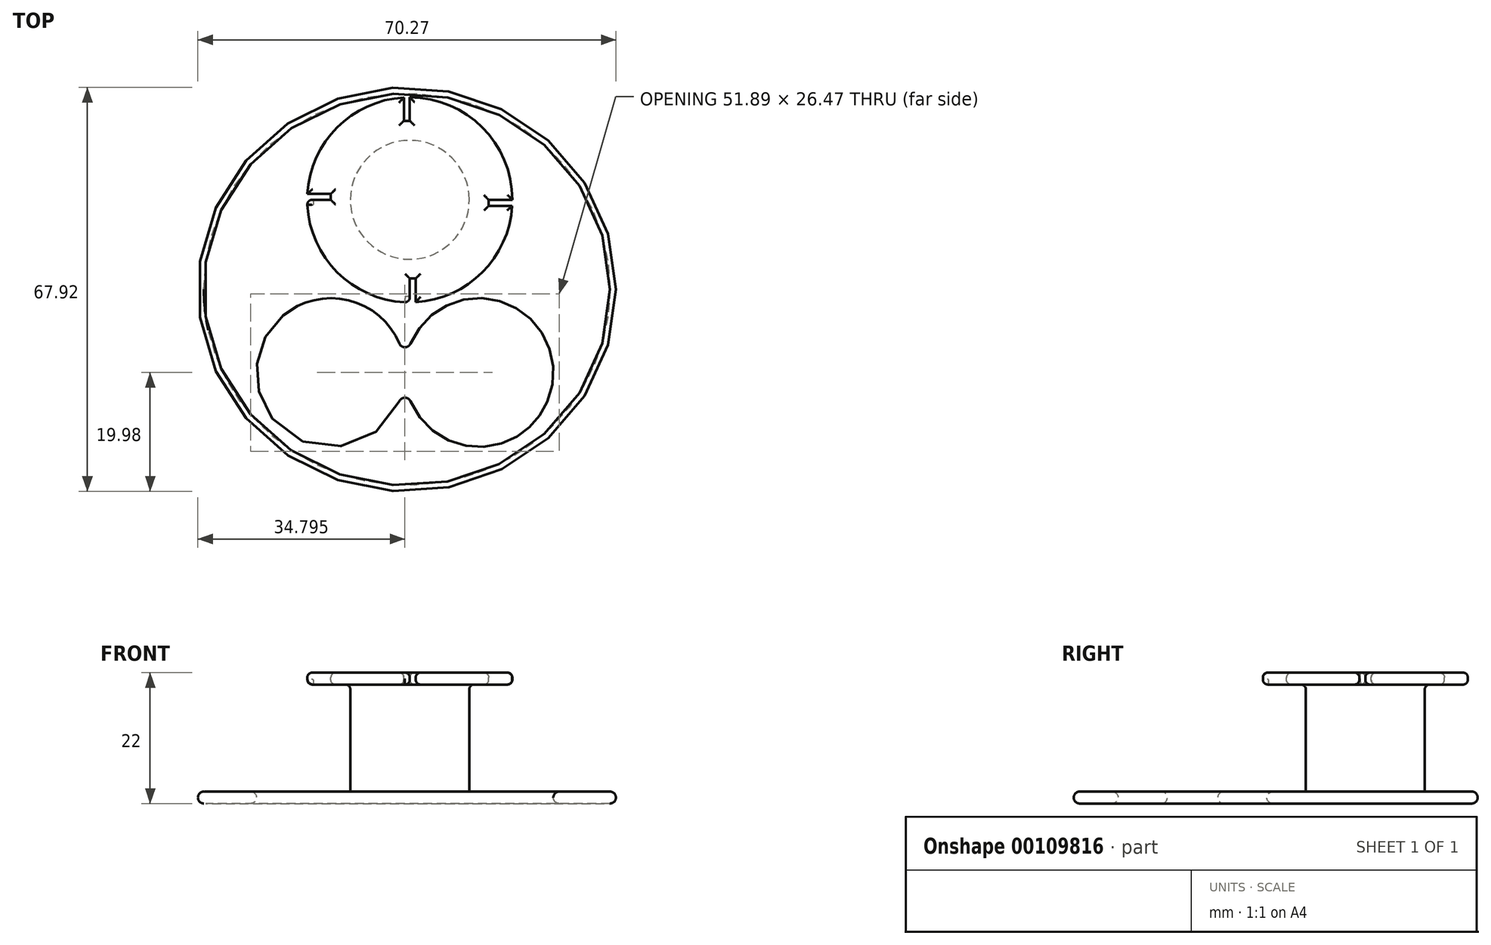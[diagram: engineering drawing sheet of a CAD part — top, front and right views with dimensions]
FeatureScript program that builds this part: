
annotation { "Feature Type Name" : "Feature", "Feature Type Description" : "" }
export const myFeature = defineFeature(function(context is Context, id is Id, definition is map)
    precondition{}
    {
        {
            var Q0;
            Q0=qCreatedBy(makeId("Top.planeOp"),FACE);
            var sketch = newSketch(context, id + "F0", { "sketchPlane" : qUnion([Q0])});
            skCircle(sketch, "E0", {"center": v(0, 0) * mm, "radius": 12.5 * mm});
            skCircle(sketch, "E1", {"center": v(24.89, 0) * mm, "radius": 12.5 * mm});
            skPoint(sketch, "E2.center.orphan", {"position": v(48.98, 0) * mm});
            skEllipse(sketch, "E3", {"center": v(12.79, 13.98) * mm, "majorRadius": 35.13 * mm, "minorRadius": 33.96 * mm, "majorAxis": v(1, 0)});
            skSolve(sketch);
        }
        {
            var Q0;
            Q0 = qSketchRegion(id + "F0", true);
            extrude(context, id + "F1", {"entities" : qUnion([Q0]), "depth" : 2 * mm});
        }
        {
            var Q0;
            Q0=makeQuery(id+"F1.opExtrude","CAP_FACE",FACE,{"disambiguationData":[OSD([sQuery(id+"F0.wireOp",EDGE,"E0"),sQuery(id+"F0.wireOp",EDGE,"E1"),sQuery(id+"F0.wireOp",EDGE,"E3")])],"isStart":false});
            var sketch = newSketch(context, id + "F2", { "sketchPlane" : qUnion([Q0])});
            skCircle(sketch, "E4", {"center": v(13.26, 29.04) * mm, "radius": 10 * mm});
            skSolve(sketch);
        }
        {
            var Q0;
            Q0 = qSketchRegion(id + "F2", true);
            extrude(context, id + "F3", {"entities" : qUnion([Q0]), "operationType" : NewBodyOperationType.ADD, "depth" : 20 * mm});
        }
        {
            var Q0;
            Q0=makeQuery(id+"F3.opExtrude","CAP_FACE",FACE,{"disambiguationData":[OSD([sQuery(id+"F2.wireOp",EDGE,"E4")])],"isStart":false});
            var sketch = newSketch(context, id + "F4", { "sketchPlane" : qUnion([Q0])});
            skArc(sketch, "E5", {"start": v(-3.97, 29.04) * mm, "mid": v(1.08, 16.85) * mm, "end": v(13.26, 11.8) * mm});
            skLineSegment(sketch, "E6.top", {"start": v(12.26, 42.33) * mm, "end": v(13.26, 42.33) * mm});
            skLineSegment(sketch, "E6.left", {"start": v(12.26, 46.25) * mm, "end": v(12.26, 42.33) * mm});
            skLineSegment(sketch, "E6.right", {"start": v(13.26, 46.16) * mm, "end": v(13.26, 42.28) * mm});
            skLineSegment(sketch, "E7.bottom", {"start": v(-3.94, 30.04) * mm, "end": v(0, 30.04) * mm});
            skLineSegment(sketch, "E7.top", {"start": v(-3.97, 29.04) * mm, "end": v(0, 29.04) * mm});
            skLineSegment(sketch, "E7.right", {"start": v(0, 30.04) * mm, "end": v(0, 29.04) * mm});
            skLineSegment(sketch, "E8.bottom", {"start": v(13.26, 15.8) * mm, "end": v(14.26, 15.8) * mm});
            skLineSegment(sketch, "E8.left", {"start": v(13.26, 15.8) * mm, "end": v(13.26, 11.8) * mm});
            skLineSegment(sketch, "E8.right", {"start": v(14.26, 15.8) * mm, "end": v(14.26, 11.83) * mm});
            skLineSegment(sketch, "E9.bottom", {"start": v(30.54, 29.04) * mm, "end": v(26.54, 29.04) * mm});
            skLineSegment(sketch, "E9.top", {"start": v(30.54, 28.04) * mm, "end": v(26.54, 28.04) * mm});
            skLineSegment(sketch, "E9.left", {"start": v(30.54, 29.04) * mm, "end": v(30.54, 28.04) * mm});
            skLineSegment(sketch, "E9.right", {"start": v(26.54, 29.04) * mm, "end": v(26.54, 28.04) * mm});
            skLineSegment(sketch, "E10", {"start": v(13.26, 29.04) * mm, "end": v(35.63, 29.04) * mm, "construction": true});
            skLineSegment(sketch, "E11", {"start": v(13.26, 29.04) * mm, "end": v(-2120.93, 29.04) * mm, "construction": true});
            skPoint(sketch, "E11.endSnap0", {"position": v(-4, 29.04) * mm});
            skLineSegment(sketch, "E12", {"start": v(13.26, 29.04) * mm, "end": v(13.26, 9.5) * mm, "construction": true});
            skLineSegment(sketch, "E13", {"start": v(13.26, 29.04) * mm, "end": v(13.26, 49.38) * mm, "construction": true});
            skLineSegment(sketch, "E14", {"start": v(13.26, 42.33) * mm, "end": v(13.26, 46.28) * mm});
            skLineSegment(sketch, "E15", {"start": v(12.16, 46.28) * mm, "end": v(12.26, 46.25) * mm});
            skLineSegment(sketch, "E16", {"start": v(-3.97, 29.04) * mm, "end": v(-3.97, 29.04) * mm});
            skArc(sketch, "E17.trimOffspring", {"start": v(30.5, 29.04) * mm, "mid": v(25.45, 41.23) * mm, "end": v(13.26, 46.28) * mm});
            skArc(sketch, "E18.trimOffspring", {"start": v(12.26, 46.25) * mm, "mid": v(1.08, 41.23) * mm, "end": v(-3.94, 30.04) * mm});
            skArc(sketch, "E19.trimOffspring", {"start": v(14.26, 11.83) * mm, "mid": v(25.45, 16.85) * mm, "end": v(30.47, 28.04) * mm});
            skSolve(sketch);
        }
        {
            var Q0;
            {var subQ6=sQuery(id+"F4.wireOp",EDGE,"E6.top");Q0=makeQuery(id+"F4.imprint","IMPRINT",FACE,{"disambiguationData":[TD([[makeQuery(id+"F4.imprint","IMPRINT",EDGE,{"derivedFrom":subQ6}),-1.0]])]});}
            extrude(context, id + "F5", {"entities" : qUnion([Q0]), "operationType" : NewBodyOperationType.ADD, "oppositeDirection" : true, "depth" : 2 * mm});
        }
        {
            var Q0;
            Q0=makeQuery(id+"F5.opExtrude","CAP_EDGE",EDGE,{"disambiguationData":[OSD([sQuery(id+"F2.wireOp",EDGE,"E4")])],"isStart":false});
            var Q1;
            {var subQ0=sQuery(id+"F4.wireOp",EDGE,"E5");Q1=makeQuery(id+"F5.opExtrude","CAP_EDGE",EDGE,{"disambiguationData":[OSD([subQ0]),TDD([makeQuery(id+"F4.imprint","IMPRINT",EDGE,{"disambiguationData":[TD([[makeQuery(id+"F4.imprint","INTERSECT",VERTEX,{"derivedFrom":[subQ0,sQuery(id+"F4.wireOp",EDGE,"E6.left"),sQuery(id+"F4.wireOp",EDGE,"E15")]}),-1.0]])],"derivedFrom":subQ0})])],"isStart":false});}
            var Q2;
            {var subQ0=sQuery(id+"F0.wireOp",EDGE,"E1");var subQ1=sQuery(id+"F0.wireOp",EDGE,"E0");Q2=makeQuery(id+"F1.opExtrude","SWEPT_EDGE",EDGE,{"disambiguationData":[OSD([subQ1,subQ0]),TDD([makeQuery(id+"F0.imprint","INTERSECT",VERTEX,{"disambiguationData":[OD(0.0)],"derivedFrom":[subQ1,subQ0]})])]});}
            var Q3;
            {var subQ0=sQuery(id+"F0.wireOp",EDGE,"E1");var subQ1=sQuery(id+"F0.wireOp",EDGE,"E0");Q3=makeQuery(id+"F1.opExtrude","SWEPT_EDGE",EDGE,{"disambiguationData":[OSD([subQ1,subQ0]),TDD([makeQuery(id+"F0.imprint","INTERSECT",VERTEX,{"disambiguationData":[OD(1.0)],"derivedFrom":[subQ1,subQ0]})])]});}
            fillet(context, id + "F6", {"entities" : qUnion([Q0, Q1, Q2, Q3]), "radius" : 1 * mm, "tangentPropagation" : true, "allowEdgeOverflow" : false});
        }
        {
            var Q0;
            Q0=makeQuery(id+"F1.opExtrude","CAP_EDGE",EDGE,{"disambiguationData":[OSD([sQuery(id+"F0.wireOp",EDGE,"E3")])],"isStart":true});
            var Q1;
            Q1=makeQuery(id+"F1.opExtrude","CAP_EDGE",EDGE,{"disambiguationData":[OSD([sQuery(id+"F0.wireOp",EDGE,"E3")])],"isStart":false});
            var Q2;
            Q2=makeQuery(id+"F1.opExtrude","CAP_EDGE",EDGE,{"disambiguationData":[OSD([sQuery(id+"F0.wireOp",EDGE,"E0")])],"isStart":true});
            var Q3;
            Q3=makeQuery(id+"F1.opExtrude","CAP_EDGE",EDGE,{"disambiguationData":[OSD([sQuery(id+"F0.wireOp",EDGE,"E1")])],"isStart":true});
            var Q4;
            Q4=makeQuery(id+"F1.opExtrude","CAP_EDGE",EDGE,{"disambiguationData":[OSD([sQuery(id+"F0.wireOp",EDGE,"E0")])],"isStart":false});
            var Q5;
            Q5=makeQuery(id+"F1.opExtrude","CAP_EDGE",EDGE,{"disambiguationData":[OSD([sQuery(id+"F0.wireOp",EDGE,"E1")])],"isStart":false});
            var Q6;
            {var subQ0=sQuery(id+"F0.wireOp",EDGE,"E1");var subQ1=sQuery(id+"F0.wireOp",EDGE,"E0");Q6=makeQuery(id+"F6.opFillet","BLEND_EDGE",EDGE,{"blendedFrom":[makeQuery(id+"F1.opExtrude","SWEPT_EDGE",EDGE,{"disambiguationData":[OSD([subQ1,subQ0]),TDD([makeQuery(id+"F0.imprint","INTERSECT",VERTEX,{"disambiguationData":[OD(1.0)],"derivedFrom":[subQ1,subQ0]})])]}),makeQuery(id+"F1.opExtrude","CAP_FACE",FACE,{"disambiguationData":[OSD([subQ1,subQ0,sQuery(id+"F0.wireOp",EDGE,"E3")])],"isStart":false})],"blendedInto":[makeQuery(id+"F1.opExtrude","CAP_FACE",FACE,{"disambiguationData":[OSD([subQ1,subQ0,sQuery(id+"F0.wireOp",EDGE,"E3")])],"isStart":false})]});}
            var Q7;
            {var subQ0=sQuery(id+"F0.wireOp",EDGE,"E1");var subQ1=sQuery(id+"F0.wireOp",EDGE,"E0");Q7=makeQuery(id+"F6.opFillet","BLEND_EDGE",EDGE,{"blendedFrom":[makeQuery(id+"F1.opExtrude","SWEPT_EDGE",EDGE,{"disambiguationData":[OSD([subQ1,subQ0]),TDD([makeQuery(id+"F0.imprint","INTERSECT",VERTEX,{"disambiguationData":[OD(1.0)],"derivedFrom":[subQ1,subQ0]})])]}),makeQuery(id+"F1.opExtrude","CAP_FACE",FACE,{"disambiguationData":[OSD([subQ1,subQ0,sQuery(id+"F0.wireOp",EDGE,"E3")])],"isStart":true})],"blendedInto":[makeQuery(id+"F1.opExtrude","CAP_FACE",FACE,{"disambiguationData":[OSD([subQ1,subQ0,sQuery(id+"F0.wireOp",EDGE,"E3")])],"isStart":true})]});}
            var Q8;
            {var subQ0=sQuery(id+"F0.wireOp",EDGE,"E1");var subQ1=sQuery(id+"F0.wireOp",EDGE,"E0");Q8=makeQuery(id+"F6.opFillet","BLEND_EDGE",EDGE,{"blendedFrom":[makeQuery(id+"F1.opExtrude","SWEPT_EDGE",EDGE,{"disambiguationData":[OSD([subQ1,subQ0]),TDD([makeQuery(id+"F0.imprint","INTERSECT",VERTEX,{"disambiguationData":[OD(0.0)],"derivedFrom":[subQ1,subQ0]})])]}),makeQuery(id+"F1.opExtrude","CAP_FACE",FACE,{"disambiguationData":[OSD([subQ1,subQ0,sQuery(id+"F0.wireOp",EDGE,"E3")])],"isStart":false})],"blendedInto":[makeQuery(id+"F1.opExtrude","CAP_FACE",FACE,{"disambiguationData":[OSD([subQ1,subQ0,sQuery(id+"F0.wireOp",EDGE,"E3")])],"isStart":false})]});}
            var Q9;
            {var subQ0=sQuery(id+"F0.wireOp",EDGE,"E1");var subQ1=sQuery(id+"F0.wireOp",EDGE,"E0");Q9=makeQuery(id+"F6.opFillet","BLEND_EDGE",EDGE,{"blendedFrom":[makeQuery(id+"F1.opExtrude","SWEPT_EDGE",EDGE,{"disambiguationData":[OSD([subQ1,subQ0]),TDD([makeQuery(id+"F0.imprint","INTERSECT",VERTEX,{"disambiguationData":[OD(0.0)],"derivedFrom":[subQ1,subQ0]})])]}),makeQuery(id+"F1.opExtrude","CAP_FACE",FACE,{"disambiguationData":[OSD([subQ1,subQ0,sQuery(id+"F0.wireOp",EDGE,"E3")])],"isStart":true})],"blendedInto":[makeQuery(id+"F1.opExtrude","CAP_FACE",FACE,{"disambiguationData":[OSD([subQ1,subQ0,sQuery(id+"F0.wireOp",EDGE,"E3")])],"isStart":true})]});}
            fillet(context, id + "F7", {"entities" : qUnion([Q0, Q1, Q2, Q3, Q4, Q5, Q6, Q7, Q8, Q9]), "radius" : 1 * mm, "tangentPropagation" : true, "allowEdgeOverflow" : false});
        }
        {
            var Q0;
            Q0=makeQuery(id+"F5.opExtrude","CAP_FACE",FACE,{"disambiguationData":[OSD([sQuery(id+"F2.wireOp",EDGE,"E4"),sQuery(id+"F4.wireOp",EDGE,"E5"),sQuery(id+"F4.wireOp",EDGE,"E6.top"),sQuery(id+"F4.wireOp",EDGE,"E6.left"),sQuery(id+"F4.wireOp",EDGE,"E7.bottom"),sQuery(id+"F4.wireOp",EDGE,"E7.top"),sQuery(id+"F4.wireOp",EDGE,"E7.right"),sQuery(id+"F4.wireOp",EDGE,"E8.bottom"),sQuery(id+"F4.wireOp",EDGE,"E8.left"),sQuery(id+"F4.wireOp",EDGE,"E8.right"),sQuery(id+"F4.wireOp",EDGE,"E9.bottom"),sQuery(id+"F4.wireOp",EDGE,"E9.top"),sQuery(id+"F4.wireOp",EDGE,"E9.right"),sQuery(id+"F4.wireOp",EDGE,"E14"),sQuery(id+"F4.wireOp",EDGE,"E17.trimOffspring"),sQuery(id+"F4.wireOp",EDGE,"E18.trimOffspring"),sQuery(id+"F4.wireOp",EDGE,"E19.trimOffspring")])],"isStart":false});
            var Q1;
            {var subQ0=sQuery(id+"F2.wireOp",EDGE,"E4");Q1=makeQuery(id+"F5.boolean.opBoolean","MERGE",FACE,{"derivedFrom":[makeQuery(id+"F3.opExtrude","CAP_FACE",FACE,{"disambiguationData":[OSD([subQ0])],"isStart":false}),makeQuery(id+"F5.opExtrude","CAP_FACE",FACE,{"disambiguationData":[OSD([subQ0,sQuery(id+"F4.wireOp",EDGE,"E5"),sQuery(id+"F4.wireOp",EDGE,"E6.top"),sQuery(id+"F4.wireOp",EDGE,"E6.left"),sQuery(id+"F4.wireOp",EDGE,"E7.bottom"),sQuery(id+"F4.wireOp",EDGE,"E7.top"),sQuery(id+"F4.wireOp",EDGE,"E7.right"),sQuery(id+"F4.wireOp",EDGE,"E8.bottom"),sQuery(id+"F4.wireOp",EDGE,"E8.left"),sQuery(id+"F4.wireOp",EDGE,"E8.right"),sQuery(id+"F4.wireOp",EDGE,"E9.bottom"),sQuery(id+"F4.wireOp",EDGE,"E9.top"),sQuery(id+"F4.wireOp",EDGE,"E9.right"),sQuery(id+"F4.wireOp",EDGE,"E14"),sQuery(id+"F4.wireOp",EDGE,"E17.trimOffspring"),sQuery(id+"F4.wireOp",EDGE,"E18.trimOffspring"),sQuery(id+"F4.wireOp",EDGE,"E19.trimOffspring")])],"isStart":true})]});}
            fillet(context, id + "F8", {"entities" : qUnion([Q0, Q1]), "radius" : 0.8 * mm, "tangentPropagation" : true, "allowEdgeOverflow" : false});
        }
    });
